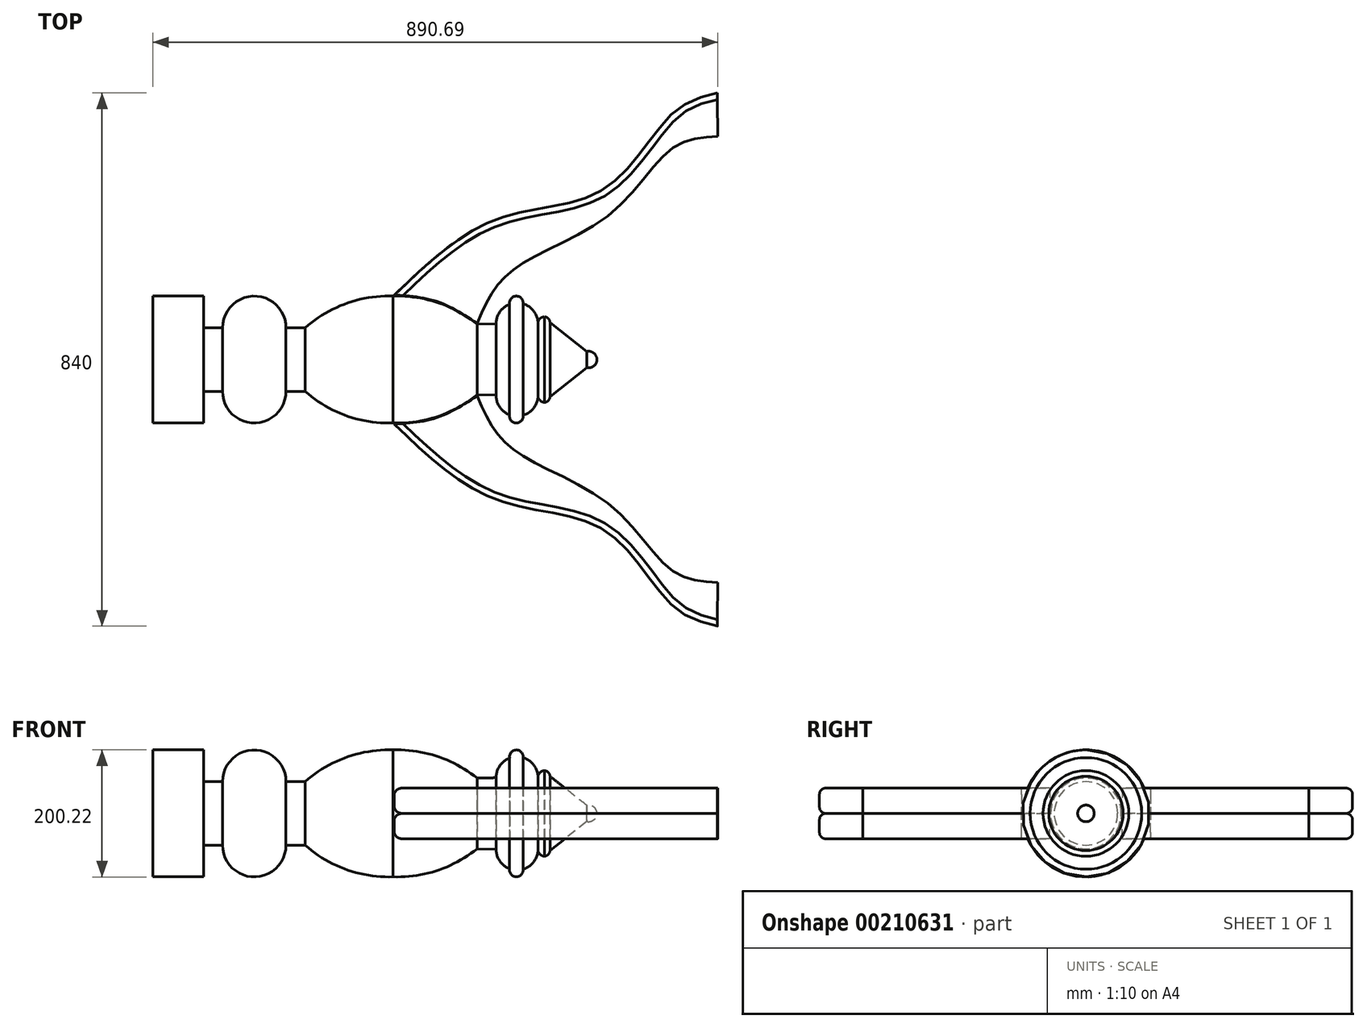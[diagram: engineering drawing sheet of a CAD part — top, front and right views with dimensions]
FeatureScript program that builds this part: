
annotation { "Feature Type Name" : "Feature", "Feature Type Description" : "" }
export const myFeature = defineFeature(function(context is Context, id is Id, definition is map)
    precondition{}
    {
        {
            var Q0;
            Q0=qCreatedBy(makeId("Top.planeOp"),FACE);
            var sketch = newSketch(context, id + "F0", { "sketchPlane" : qUnion([Q0])});
            skLineSegment(sketch, "E0", {"start": v(-718.7, 0) * mm, "end": v(0, 0) * mm, "construction": true});
            skLineSegment(sketch, "E1.bottom", {"start": v(-700, 100) * mm, "end": v(-620, 100) * mm});
            skLineSegment(sketch, "E1.top", {"start": v(-700, 0) * mm, "end": v(0, 0) * mm});
            skLineSegment(sketch, "E1.left", {"start": v(-700, 100) * mm, "end": v(-700, 0) * mm});
            skLineSegment(sketch, "E1.right", {"start": v(0, 58.59) * mm, "end": v(0, 0) * mm});
            skLineSegment(sketch, "E2", {"start": v(-620, 100) * mm, "end": v(-620, 0) * mm});
            skLineSegment(sketch, "E3", {"start": v(-620, 50) * mm, "end": v(-590, 50) * mm});
            skLineSegment(sketch, "E4.bottom", {"start": v(-620, 50) * mm, "end": v(-586.8, 50) * mm});
            skLineSegment(sketch, "E4.top", {"start": v(-620, 0) * mm, "end": v(-590, 0) * mm});
            skLineSegment(sketch, "E4.left", {"start": v(-620, 50) * mm, "end": v(-620, 0) * mm});
            skArc(sketch, "E5", {"start": v(-490, 50) * mm, "mid": v(-540, 100) * mm, "end": v(-590, 50) * mm});
            skLineSegment(sketch, "E6.bottom", {"start": v(-490, 50) * mm, "end": v(-460, 50) * mm});
            skLineSegment(sketch, "E6.top", {"start": v(-590, 0) * mm, "end": v(-460, 0) * mm});
            skLineSegment(sketch, "E6.left", {"start": v(-590, 50) * mm, "end": v(-590, 0) * mm});
            skLineSegment(sketch, "E6.right", {"start": v(-460, 50) * mm, "end": v(-460, 0) * mm});
            skLineSegment(sketch, "E7.top", {"start": v(-490, 0) * mm, "end": v(-460, 0) * mm});
            skLineSegment(sketch, "E7.left", {"start": v(-490, 50) * mm, "end": v(-490, 0) * mm});
            skArc(sketch, "E8", {"start": v(-321.11, 100) * mm, "mid": v(-395.34, 88.28) * mm, "end": v(-460, 50) * mm});
            skLineSegment(sketch, "E9", {"start": v(-188.9, 55.64) * mm, "end": v(-158.9, 56.26) * mm});
            skArc(sketch, "E10.MirrorCS", {"start": v(-321.11, 100) * mm, "mid": v(-251.01, 89.72) * mm, "end": v(-188.9, 55.64) * mm});
            skLineSegment(sketch, "E11.trimOffspring", {"start": v(-321.11, 100) * mm, "end": v(-308.15, 100) * mm});
            skPoint(sketch, "E12.start.orphan", {"position": v(-169.1, 50) * mm});
            skLineSegment(sketch, "E13.bottom", {"start": v(-188.9, 55.64) * mm, "end": v(-158.9, 55.64) * mm});
            skLineSegment(sketch, "E13.top", {"start": v(-188.9, 0) * mm, "end": v(-158.9, 0) * mm});
            skLineSegment(sketch, "E13.left", {"start": v(-188.9, 55.64) * mm, "end": v(-188.9, 0) * mm});
            skLineSegment(sketch, "E13.right", {"start": v(-158.9, 55.64) * mm, "end": v(-158.9, 0) * mm});
            skLineSegment(sketch, "E14.top", {"start": v(0, 0) * mm, "end": v(-158.9, 0) * mm});
            skLineSegment(sketch, "E14.right", {"start": v(-158.9, 58.59) * mm, "end": v(-158.9, 0) * mm});
            skArc(sketch, "E15", {"start": v(-158.9, 56.26) * mm, "mid": v(-153.03, 75.05) * mm, "end": v(-137.52, 87.18) * mm});
            skArc(sketch, "E16", {"start": v(-127.01, 100) * mm, "mid": v(-135.3, 96.08) * mm, "end": v(-137.52, 87.18) * mm});
            skArc(sketch, "E17.MirrorCS", {"start": v(-127.77, 99.97) * mm, "mid": v(-119.22, 96.64) * mm, "end": v(-116.39, 87.92) * mm});
            skArc(sketch, "E18.MirrorCS", {"start": v(-92.89, 58.59) * mm, "mid": v(-100.06, 76.92) * mm, "end": v(-116.39, 87.92) * mm});
            skArc(sketch, "E19", {"start": v(-82.72, 67.55) * mm, "mid": v(-89.3, 64.76) * mm, "end": v(-92.89, 58.59) * mm});
            skArc(sketch, "E20", {"start": v(-92.89, 58.59) * mm, "mid": v(-92.87, 57.42) * mm, "end": v(-92.71, 56.26) * mm});
            skLineSegment(sketch, "E21.bottom", {"start": v(-92.89, 56.26) * mm, "end": v(-92.71, 56.26) * mm});
            skLineSegment(sketch, "E21.top", {"start": v(-158.9, 0) * mm, "end": v(0, 0) * mm});
            skLineSegment(sketch, "E21.left", {"start": v(-158.9, 56.26) * mm, "end": v(-158.9, 0) * mm});
            skLineSegment(sketch, "E21.right", {"start": v(0, 56.26) * mm, "end": v(0, 0) * mm});
            skLineSegment(sketch, "E22.top", {"start": v(-158.9, 58.59) * mm, "end": v(-158.81, 58.59) * mm});
            skLineSegment(sketch, "E22.left", {"start": v(-158.9, 56.26) * mm, "end": v(-158.9, 58.59) * mm});
            skLineSegment(sketch, "E22.right", {"start": v(-92.89, 56.26) * mm, "end": v(-92.89, 58.59) * mm});
            skLineSegment(sketch, "E23.top", {"start": v(-158.9, 0) * mm, "end": v(-92.89, 0) * mm});
            skLineSegment(sketch, "E23.right", {"start": v(-92.89, 58.59) * mm, "end": v(-92.89, 0) * mm});
            skLineSegment(sketch, "E24.bottom", {"start": v(-73.99, 58.59) * mm, "end": v(-73.95, 58.59) * mm});
            skLineSegment(sketch, "E24.top", {"start": v(-92.89, 0) * mm, "end": v(0, 0) * mm});
            skLineSegment(sketch, "E25.top", {"start": v(0, 0) * mm, "end": v(-73.95, 0) * mm});
            skLineSegment(sketch, "E25.left", {"start": v(0, 58.59) * mm, "end": v(0, 56.26) * mm});
            skLineSegment(sketch, "E25.right", {"start": v(-73.95, 58.59) * mm, "end": v(-73.95, 0) * mm});
            skArc(sketch, "E26.trimOffspring", {"start": v(-74.16, 56.26) * mm, "mid": v(-75.9, 63.83) * mm, "end": v(-82.72, 67.55) * mm});
            skLineSegment(sketch, "E27.trimOffspring", {"start": v(-74.16, 56.26) * mm, "end": v(-73.95, 56.26) * mm});
            skLineSegment(sketch, "E28", {"start": v(-73.95, 58.59) * mm, "end": v(-16.1, 12.75) * mm});
            skArc(sketch, "E29", {"start": v(0, 0) * mm, "mid": v(-4.97, 10.27) * mm, "end": v(-16.1, 12.75) * mm});
            skLineSegment(sketch, "E30.top", {"start": v(-16.1, 0) * mm, "end": v(-73.95, 0) * mm});
            skLineSegment(sketch, "E30.left", {"start": v(-16.1, 12.75) * mm, "end": v(-16.1, 0) * mm});
            skLineSegment(sketch, "E30.right", {"start": v(-73.95, 12.75) * mm, "end": v(-73.95, 0) * mm});
            skSolve(sketch);
        }
        {
            var Q0;
            Q0 = qSketchRegion(id + "F0", true);
            var Q1;
            Q1=sQuery(id+"F0.wireOp",EDGE,"E0");
            revolve(context, id + "F1", {"surfaceOperationType" : NewSurfaceOperationType.NEW, "entities" : qUnion([Q0]), "axis" : qUnion([Q1]), "revolveType" : RevolveType.FULL});
        }
        {
            var Q0;
            Q0=qCreatedBy(makeId("Top.planeOp"),FACE);
            var sketch = newSketch(context, id + "F2", { "sketchPlane" : qUnion([Q0])});
            skLineSegment(sketch, "E31", {"start": v(-319.2, 0) * mm, "end": v(191.04, 0) * mm, "construction": true});
            skLineSegment(sketch, "E32.left", {"start": v(-319.2, 0) * mm, "end": v(-319.2, 101.72) * mm});
            skLineSegment(sketch, "E33.0", {"start": v(-700, -100) * mm, "end": v(-700, 100) * mm});
            skFitSpline(sketch, "E34", {"points": [v(-319.2, 101.72) * mm, v(-156.5, 221.48) * mm, v(12.71, 269.64) * mm, v(119.45, 388.08) * mm, v(190, 420) * mm], "startDerivative": vector(526.26, 504.76) * mm, "endDerivative": vector(401.14, 91.11) * mm});
            skFitSpline(sketch, "E35.MirrorCS", {"points": [v(-319.2, -101.72) * mm, v(-156.5, -221.48) * mm, v(12.71, -269.64) * mm, v(119.45, -388.08) * mm, v(190, -420) * mm], "startDerivative": vector(526.26, -504.76) * mm, "endDerivative": vector(401.14, -91.11) * mm});
            skFitSpline(sketch, "E36", {"points": [v(-188.51, 57.3) * mm, v(-158.14, 115.28) * mm, v(-102, 160.38) * mm, v(28.7, 235.85) * mm, v(119.82, 333.42) * mm, v(190.69, 351.58) * mm], "startDerivative": vector(161.12, 373.46) * mm, "endDerivative": vector(421.93, 22.56) * mm});
            skFitSpline(sketch, "E37.MirrorCS", {"points": [v(-188.51, -57.3) * mm, v(-158.14, -115.28) * mm, v(-102, -160.38) * mm, v(28.7, -235.85) * mm, v(119.82, -333.42) * mm, v(190.69, -351.58) * mm], "startDerivative": vector(161.12, -373.46) * mm, "endDerivative": vector(421.93, -22.56) * mm});
            skFitSpline(sketch, "E38", {"points": [v(-319.2, 101.72) * mm, v(-253.44, 91.92) * mm, v(-188.51, 57.3) * mm], "startDerivative": vector(136.97, -8.58) * mm, "endDerivative": vector(124.5, -79.68) * mm});
            skFitSpline(sketch, "E39.MirrorCS", {"points": [v(-319.2, -101.72) * mm, v(-253.44, -91.92) * mm, v(-188.51, -57.3) * mm], "startDerivative": vector(136.97, 8.58) * mm, "endDerivative": vector(124.5, 79.68) * mm});
            skLineSegment(sketch, "E40", {"start": v(190, 420) * mm, "end": v(190.69, 351.58) * mm});
            skPoint(sketch, "E32.right.end.orphan", {"position": v(190, 297.65) * mm});
            skLineSegment(sketch, "E41", {"start": v(190.69, -351.58) * mm, "end": v(190, -420) * mm});
            skSolve(sketch);
        }
        {
            var Q0;
            Q0 = qSketchRegion(id + "F2", true);
            extrude(context, id + "F3", {"entities" : qUnion([Q0]), "depth" : 40 * mm, "offsetDistance" : 25 * mm});
        }
        {
            var Q0;
            Q0 = qSketchRegion(id + "F2", true);
            extrude(context, id + "F4", {"entities" : qUnion([Q0]), "oppositeDirection" : true, "depth" : 40 * mm, "offsetDistance" : 25 * mm});
        }
        {
            var Q0;
            Q0=makeQuery(id+"F3.opExtrude","CAP_EDGE",EDGE,{"disambiguationData":[OSD([sQuery(id+"F2.wireOp",EDGE,"E34")])],"isStart":false});
            var Q1;
            Q1=makeQuery(id+"F4.opExtrude","CAP_EDGE",EDGE,{"disambiguationData":[OSD([sQuery(id+"F2.wireOp",EDGE,"E34")])],"isStart":false});
            var Q2;
            Q2=makeQuery(id+"F3.opExtrude","CAP_EDGE",EDGE,{"disambiguationData":[OSD([sQuery(id+"F2.wireOp",EDGE,"E34")])],"isStart":true});
            fillet(context, id + "F5", {"entities" : qUnion([Q0, Q1, Q2]), "radius" : 10 * mm, "tangentPropagation" : true, "allowEdgeOverflow" : false});
        }
        {
            var Q0;
            Q0=makeQuery(id+"F4.opExtrude","CAP_EDGE",EDGE,{"disambiguationData":[OSD([sQuery(id+"F2.wireOp",EDGE,"E34")])],"isStart":true});
            fillet(context, id + "F6", {"entities" : qUnion([Q0]), "radius" : 10 * mm, "tangentPropagation" : true, "allowEdgeOverflow" : false});
        }
        {
            var Q0;
            Q0=makeQuery(id+"F4.opExtrude","CAP_EDGE",EDGE,{"disambiguationData":[OSD([sQuery(id+"F2.wireOp",EDGE,"E35.MirrorCS")])],"isStart":false});
            var Q1;
            Q1=makeQuery(id+"F3.opExtrude","CAP_EDGE",EDGE,{"disambiguationData":[OSD([sQuery(id+"F2.wireOp",EDGE,"E35.MirrorCS")])],"isStart":true});
            var Q2;
            Q2=makeQuery(id+"F3.opExtrude","CAP_EDGE",EDGE,{"disambiguationData":[OSD([sQuery(id+"F2.wireOp",EDGE,"E35.MirrorCS")])],"isStart":false});
            fillet(context, id + "F7", {"entities" : qUnion([Q0, Q1, Q2]), "radius" : 10 * mm, "tangentPropagation" : true, "allowEdgeOverflow" : false});
        }
        {
            var Q0;
            Q0=makeQuery(id+"F4.opExtrude","CAP_EDGE",EDGE,{"disambiguationData":[OSD([sQuery(id+"F2.wireOp",EDGE,"E35.MirrorCS")])],"isStart":true});
            fillet(context, id + "F8", {"entities" : qUnion([Q0]), "radius" : 10 * mm, "tangentPropagation" : true, "allowEdgeOverflow" : false});
        }
    });
